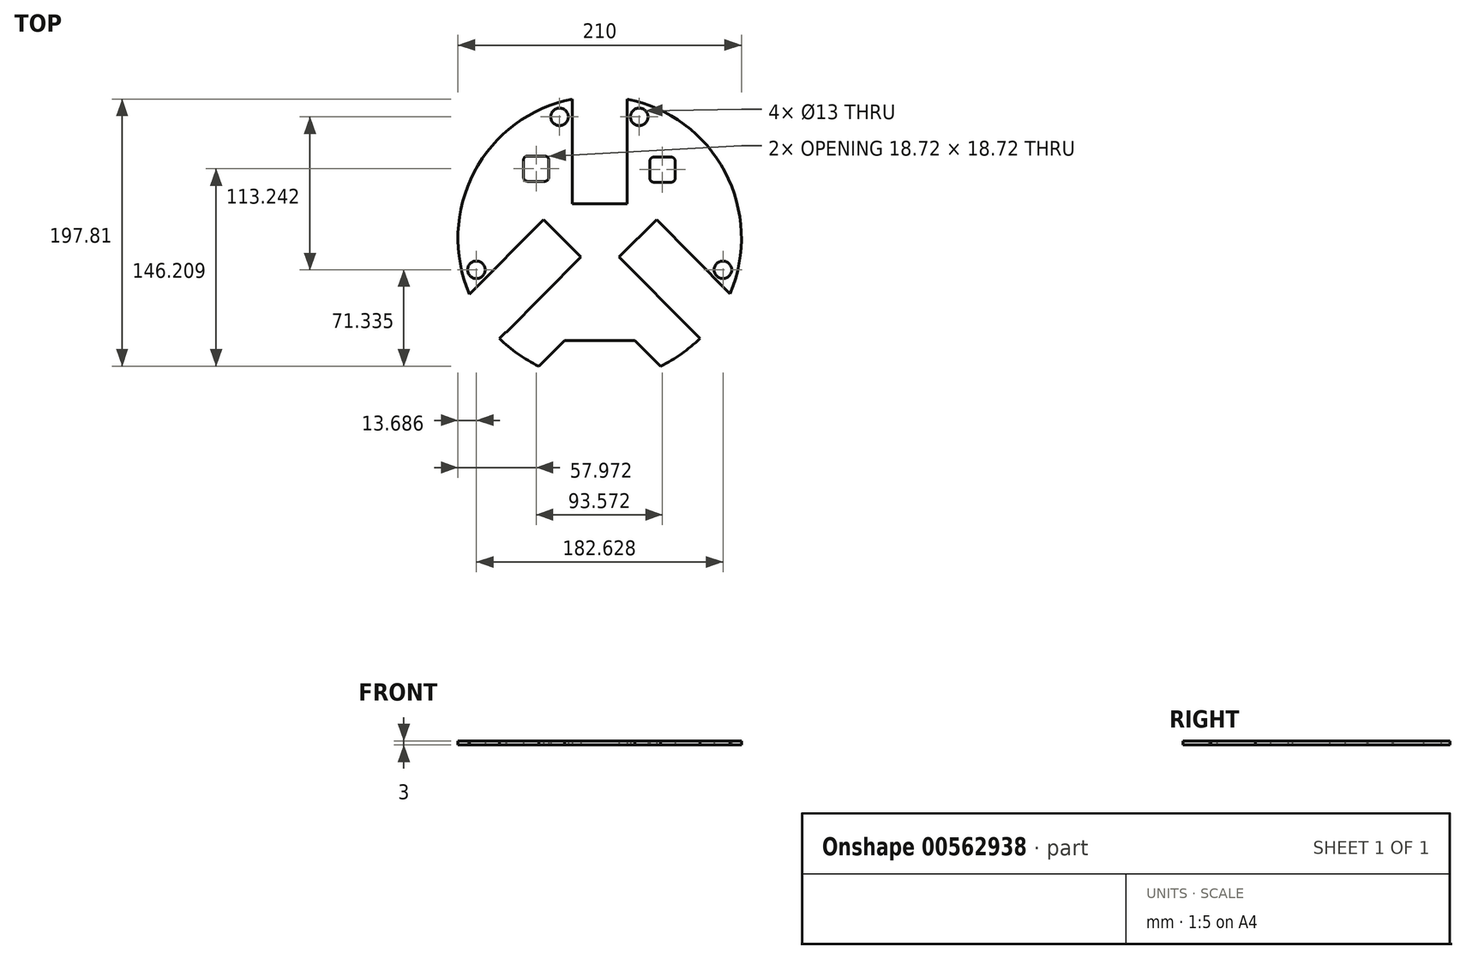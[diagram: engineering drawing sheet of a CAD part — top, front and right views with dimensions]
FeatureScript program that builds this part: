
annotation { "Feature Type Name" : "Feature", "Feature Type Description" : "" }
export const myFeature = defineFeature(function(context is Context, id is Id, definition is map)
    precondition{}
    {
        {
            var Q0;
            Q0=qCreatedBy(makeId("Top.planeOp"),FACE);
            var sketch = newSketch(context, id + "F0", { "sketchPlane" : qUnion([Q0])});
            skCircle(sketch, "E0", {"center": v(0, 0) * mm, "radius": 105 * mm});
            skLineSegment(sketch, "E1", {"start": v(0, 105) * mm, "end": v(0, -105) * mm});
            skLineSegment(sketch, "E2", {"start": v(0, 0) * mm, "end": v(-74.25, -74.25) * mm});
            skLineSegment(sketch, "E3", {"start": v(0, 0) * mm, "end": v(74.25, -74.25) * mm});
            skLineSegment(sketch, "E4", {"start": v(0, 0) * mm, "end": v(0, 105) * mm});
            skLineSegment(sketch, "E5", {"start": v(0, -49.67) * mm, "end": v(-45.13, -94.8) * mm});
            skLineSegment(sketch, "E6", {"start": v(0, -49.67) * mm, "end": v(45.13, -94.8) * mm});
            skLineSegment(sketch, "E7", {"start": v(-20.43, 103.99) * mm, "end": v(-0.4, 103.99) * mm});
            skLineSegment(sketch, "E8.bottom", {"start": v(-20.43, 103.99) * mm, "end": v(20.33, 103.99) * mm});
            skLineSegment(sketch, "E8.top", {"start": v(-20.43, 25.29) * mm, "end": v(20.33, 25.29) * mm});
            skLineSegment(sketch, "E8.left", {"start": v(-20.43, 103.99) * mm, "end": v(-20.43, 25.29) * mm});
            skLineSegment(sketch, "E8.right", {"start": v(20.33, 103.99) * mm, "end": v(20.33, 25.29) * mm});
            skLineSegment(sketch, "E9.bottom", {"start": v(-41.67, 13.74) * mm, "end": v(-13.83, -13.93) * mm});
            skLineSegment(sketch, "E9.top", {"start": v(-97.14, -42.09) * mm, "end": v(-69.3, -69.75) * mm});
            skLineSegment(sketch, "E9.left", {"start": v(-41.67, 13.74) * mm, "end": v(-97.14, -42.09) * mm});
            skLineSegment(sketch, "E9.right", {"start": v(-13.83, -13.93) * mm, "end": v(-69.3, -69.75) * mm});
            skLineSegment(sketch, "E10.bottom", {"start": v(14.3, -13.9) * mm, "end": v(42.15, 13.74) * mm});
            skLineSegment(sketch, "E10.top", {"start": v(69.75, -69.75) * mm, "end": v(97.6, -42.1) * mm});
            skLineSegment(sketch, "E10.left", {"start": v(14.3, -13.9) * mm, "end": v(69.75, -69.75) * mm});
            skLineSegment(sketch, "E10.right", {"start": v(42.15, 13.74) * mm, "end": v(97.6, -42.1) * mm});
            skLineSegment(sketch, "E11.bottom", {"start": v(-53.39, 60.77) * mm, "end": v(-40.67, 60.77) * mm});
            skLineSegment(sketch, "E11.top", {"start": v(-53.39, 42.05) * mm, "end": v(-40.67, 42.05) * mm});
            skLineSegment(sketch, "E11.left", {"start": v(-56.39, 57.77) * mm, "end": v(-56.39, 45.05) * mm});
            skLineSegment(sketch, "E11.right", {"start": v(-37.67, 57.77) * mm, "end": v(-37.67, 45.05) * mm});
            skLineSegment(sketch, "E12.bottom", {"start": v(40.18, 60.07) * mm, "end": v(52.9, 60.07) * mm});
            skLineSegment(sketch, "E12.top", {"start": v(40.18, 41.35) * mm, "end": v(52.9, 41.35) * mm});
            skLineSegment(sketch, "E12.left", {"start": v(37.18, 57.07) * mm, "end": v(37.18, 44.35) * mm});
            skLineSegment(sketch, "E12.right", {"start": v(55.9, 57.07) * mm, "end": v(55.9, 44.35) * mm});
            skCircle(sketch, "E13", {"center": v(-29.72, 89.78) * mm, "radius": 6.5 * mm});
            skCircle(sketch, "E14", {"center": v(29.3, 89.78) * mm, "radius": 6.5 * mm});
            skCircle(sketch, "E15", {"center": v(-91.31, -23.47) * mm, "radius": 6.5 * mm});
            skCircle(sketch, "E16", {"center": v(91.31, -23.47) * mm, "radius": 6.5 * mm});
            skPoint(sketch, "E17.visualSharp", {"position": v(-56.39, 60.77) * mm});
            skArc(sketch, "E17.filletArc", {"start": v(-53.39, 60.77) * mm, "mid": v(-55.5, 59.89) * mm, "end": v(-56.39, 57.77) * mm});
            skPoint(sketch, "E18.visualSharp", {"position": v(-37.67, 60.77) * mm});
            skArc(sketch, "E18.filletArc", {"start": v(-37.67, 57.77) * mm, "mid": v(-38.55, 59.89) * mm, "end": v(-40.67, 60.77) * mm});
            skPoint(sketch, "E19.visualSharp", {"position": v(-37.67, 42.05) * mm});
            skArc(sketch, "E19.filletArc", {"start": v(-40.67, 42.05) * mm, "mid": v(-38.55, 42.93) * mm, "end": v(-37.67, 45.05) * mm});
            skPoint(sketch, "E20.visualSharp", {"position": v(-56.39, 42.05) * mm});
            skArc(sketch, "E20.filletArc", {"start": v(-56.39, 45.05) * mm, "mid": v(-55.5, 42.93) * mm, "end": v(-53.39, 42.05) * mm});
            skPoint(sketch, "E21.visualSharp", {"position": v(37.18, 60.07) * mm});
            skArc(sketch, "E21.filletArc", {"start": v(40.18, 60.07) * mm, "mid": v(38.06, 59.19) * mm, "end": v(37.18, 57.07) * mm});
            skPoint(sketch, "E22.visualSharp", {"position": v(55.9, 60.07) * mm});
            skArc(sketch, "E22.filletArc", {"start": v(55.9, 57.07) * mm, "mid": v(55.03, 59.19) * mm, "end": v(52.9, 60.07) * mm});
            skPoint(sketch, "E23.visualSharp", {"position": v(55.9, 41.35) * mm});
            skArc(sketch, "E23.filletArc", {"start": v(52.9, 41.35) * mm, "mid": v(55.03, 42.23) * mm, "end": v(55.9, 44.35) * mm});
            skPoint(sketch, "E24.visualSharp", {"position": v(37.18, 41.35) * mm});
            skArc(sketch, "E24.filletArc", {"start": v(37.18, 44.35) * mm, "mid": v(38.06, 42.23) * mm, "end": v(40.18, 41.35) * mm});
            skLineSegment(sketch, "E25", {"start": v(0, -49.67) * mm, "end": v(0, -64.72) * mm});
            skLineSegment(sketch, "E26", {"start": v(-26.12, -75.8) * mm, "end": v(26.12, -75.8) * mm});
            skSolve(sketch);
        }
        {
            var Q0;
            Q0=makeQuery(id+"F0.imprint","IMPRINT",FACE,{"disambiguationData":[TD([[makeQuery(id+"F0.imprint","IMPRINT",EDGE,{"derivedFrom":sQuery(id+"F0.wireOp",EDGE,"E11.bottom")}),1.0]])]});
            var Q1;
            {var subQ9=sQuery(id+"F0.wireOp",EDGE,"E10.bottom");Q1=makeQuery(id+"F0.imprint","IMPRINT",FACE,{"disambiguationData":[TD([[makeQuery(id+"F0.imprint","IMPRINT",EDGE,{"derivedFrom":subQ9}),1.0]])]});}
            var Q2;
            {var subQ5=sQuery(id+"F0.wireOp",EDGE,"E9.right");Q2=makeQuery(id+"F0.imprint","IMPRINT",FACE,{"disambiguationData":[TD([[makeQuery(id+"F0.imprint","IMPRINT",EDGE,{"derivedFrom":subQ5}),1.0]])]});}
            var Q3;
            {var subQ0=sQuery(id+"F0.wireOp",EDGE,"E3");var subQ4=sQuery(id+"F0.wireOp",EDGE,"E0");var subQ5=makeQuery(id+"F0.imprint","INTERSECT",VERTEX,{"derivedFrom":[subQ4,subQ0]});Q3=makeQuery(id+"F0.imprint","IMPRINT",FACE,{"disambiguationData":[TD([[makeQuery(id+"F0.imprint","IMPRINT",EDGE,{"disambiguationData":[TD([[subQ5,1.0]])],"derivedFrom":subQ4}),1.0]])]});}
            var Q4;
            {var subQ1=sQuery(id+"F0.wireOp",EDGE,"E1");var subQ3=makeQuery(id+"F0.imprint","IMPRINT",VERTEX,{"derivedFrom":subQ1});Q4=makeQuery(id+"F0.imprint","IMPRINT",FACE,{"disambiguationData":[TD([[makeQuery(id+"F0.imprint","IMPRINT",EDGE,{"disambiguationData":[TD([[subQ3,-1.0]])],"derivedFrom":subQ1}),-1.0]])]});}
            var Q5;
            {var subQ1=sQuery(id+"F0.wireOp",EDGE,"E1");var subQ3=makeQuery(id+"F0.imprint","IMPRINT",VERTEX,{"derivedFrom":subQ1});Q5=makeQuery(id+"F0.imprint","IMPRINT",FACE,{"disambiguationData":[TD([[makeQuery(id+"F0.imprint","IMPRINT",EDGE,{"disambiguationData":[TD([[subQ3,-1.0]])],"derivedFrom":subQ1}),1.0]])]});}
            extrude(context, id + "F1", {"entities" : qUnion([Q0, Q1, Q2, Q3, Q4, Q5]), "depth" : 3 * mm, "offsetDistance" : 25.4 * mm});
        }
    });
